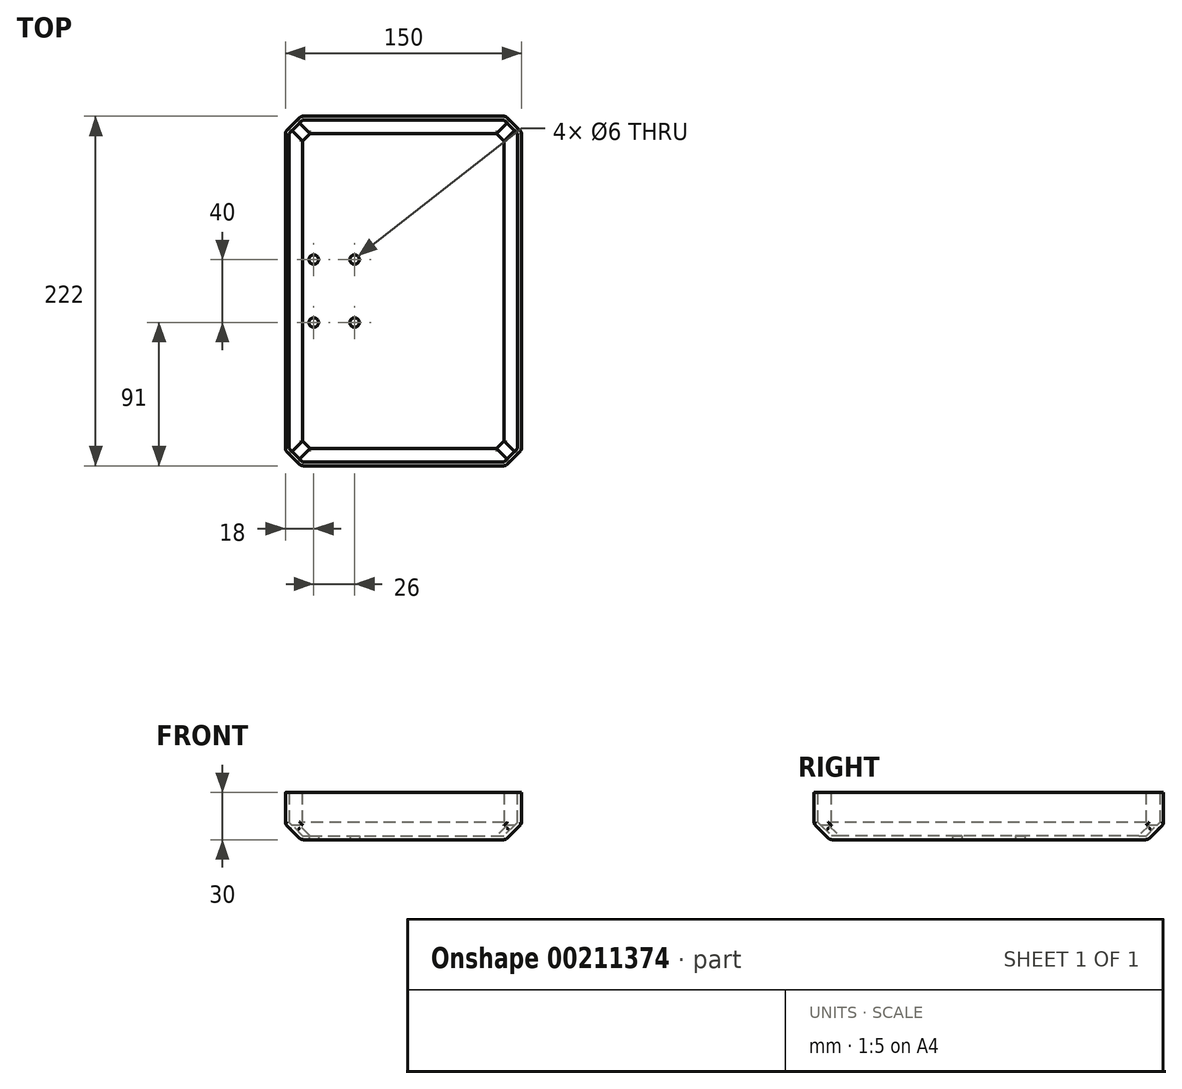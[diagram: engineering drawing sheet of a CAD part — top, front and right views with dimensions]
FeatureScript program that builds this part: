
annotation { "Feature Type Name" : "Feature", "Feature Type Description" : "" }
export const myFeature = defineFeature(function(context is Context, id is Id, definition is map)
    precondition{}
    {
        {
            var Q0;
            Q0=qCreatedBy(makeId("Front.planeOp"),FACE);
            var sketch = newSketch(context, id + "F0", { "sketchPlane" : qUnion([Q0])});
            skLineSegment(sketch, "E0.bottom", {"start": v(10, 0) * mm, "end": v(140, 0) * mm});
            skLineSegment(sketch, "E0.left", {"start": v(0, 10) * mm, "end": v(0, 30) * mm});
            skLineSegment(sketch, "E0.right", {"start": v(150, 10) * mm, "end": v(150, 30) * mm});
            skPoint(sketch, "E1.visualSharp", {"position": v(0, 0) * mm});
            skPoint(sketch, "E2.visualSharp", {"position": v(150, 0) * mm});
            skLineSegment(sketch, "E3", {"start": v(0, 30) * mm, "end": v(150, 30) * mm});
            skLineSegment(sketch, "E4", {"start": v(150, 10) * mm, "end": v(150, 0) * mm});
            skLineSegment(sketch, "E5", {"start": v(140, 0) * mm, "end": v(150, 0) * mm});
            skLineSegment(sketch, "E6", {"start": v(10, 0) * mm, "end": v(0, 0) * mm});
            skLineSegment(sketch, "E7", {"start": v(0, 10) * mm, "end": v(0, 0) * mm});
            skSolve(sketch);
        }
        {
            var Q0;
            Q0 = qSketchRegion(id + "F0", true);
            var Q1;
            Q1 = qConstructionFilter(qBodyType(qCreatedBy(id + "F0" ,EDGE), BodyType.WIRE), ConstructionObject.NO);
            extrude(context, id + "F1", {"entities" : qUnion([Q0]), "surfaceEntities" : qUnion([Q1]), "depth" : 222 * mm});
        }
        {
            var Q0;
            Q0=makeQuery(id+"F1.opExtrude","CAP_EDGE",EDGE,{"disambiguationData":[OSD([sQuery(id+"F0.wireOp",EDGE,"E0.left"),sQuery(id+"F0.wireOp",EDGE,"E7")])],"isStart":false});
            var Q1;
            Q1=makeQuery(id+"F1.opExtrude","CAP_EDGE",EDGE,{"disambiguationData":[OSD([sQuery(id+"F0.wireOp",EDGE,"E0.right"),sQuery(id+"F0.wireOp",EDGE,"E4")])],"isStart":false});
            var Q2;
            Q2=makeQuery(id+"F1.opExtrude","CAP_EDGE",EDGE,{"disambiguationData":[OSD([sQuery(id+"F0.wireOp",EDGE,"E0.right"),sQuery(id+"F0.wireOp",EDGE,"E4")])],"isStart":true});
            var Q3;
            Q3=makeQuery(id+"F1.opExtrude","CAP_EDGE",EDGE,{"disambiguationData":[OSD([sQuery(id+"F0.wireOp",EDGE,"E0.left"),sQuery(id+"F0.wireOp",EDGE,"E7")])],"isStart":true});
            chamfer(context, id + "F2", {"entities" : qUnion([Q0, Q1, Q2, Q3]), "width" : 10 * mm, "tangentPropagation" : true});
        }
        {
            var Q0;
            Q0=makeQuery(id+"F1.opExtrude","SWEPT_EDGE",EDGE,{"disambiguationData":[OSD([sQuery(id+"F0.wireOp",EDGE,"E4"),sQuery(id+"F0.wireOp",EDGE,"E5")])]});
            var Q1;
            Q1=makeQuery(id+"F1.opExtrude","CAP_EDGE",EDGE,{"disambiguationData":[OSD([sQuery(id+"F0.wireOp",EDGE,"E0.bottom"),sQuery(id+"F0.wireOp",EDGE,"E5"),sQuery(id+"F0.wireOp",EDGE,"E6")])],"isStart":false});
            var Q2;
            Q2=makeQuery(id+"F1.opExtrude","CAP_EDGE",EDGE,{"disambiguationData":[OSD([sQuery(id+"F0.wireOp",EDGE,"E0.bottom"),sQuery(id+"F0.wireOp",EDGE,"E5"),sQuery(id+"F0.wireOp",EDGE,"E6")])],"isStart":true});
            var Q3;
            Q3=makeQuery(id+"F1.opExtrude","SWEPT_EDGE",EDGE,{"disambiguationData":[OSD([sQuery(id+"F0.wireOp",EDGE,"E6"),sQuery(id+"F0.wireOp",EDGE,"E7")])]});
            chamfer(context, id + "F3", {"entities" : qUnion([Q0, Q1, Q2, Q3]), "width" : 10 * mm, "tangentPropagation" : true});
        }
        {
            var Q0;
            {var subQ0=sQuery(id+"F0.wireOp",EDGE,"E6");Q0=makeQuery(id+"F3.opChamfer","BLEND_EDGE",EDGE,{"blendedFrom":[makeQuery(id+"F1.opExtrude","SWEPT_EDGE",EDGE,{"disambiguationData":[OSD([subQ0,sQuery(id+"F0.wireOp",EDGE,"E7")])]}),makeQuery(id+"F1.opExtrude","CAP_EDGE",EDGE,{"disambiguationData":[OSD([sQuery(id+"F0.wireOp",EDGE,"E0.bottom"),sQuery(id+"F0.wireOp",EDGE,"E5"),subQ0])],"isStart":false})],"blendedInto":[]});}
            var Q1;
            {var subQ0=sQuery(id+"F0.wireOp",EDGE,"E5");Q1=makeQuery(id+"F3.opChamfer","BLEND_EDGE",EDGE,{"blendedFrom":[makeQuery(id+"F1.opExtrude","SWEPT_EDGE",EDGE,{"disambiguationData":[OSD([sQuery(id+"F0.wireOp",EDGE,"E4"),subQ0])]}),makeQuery(id+"F1.opExtrude","CAP_EDGE",EDGE,{"disambiguationData":[OSD([sQuery(id+"F0.wireOp",EDGE,"E0.bottom"),subQ0,sQuery(id+"F0.wireOp",EDGE,"E6")])],"isStart":false})],"blendedInto":[]});}
            var Q2;
            {var subQ0=sQuery(id+"F0.wireOp",EDGE,"E5");Q2=makeQuery(id+"F3.opChamfer","BLEND_EDGE",EDGE,{"blendedFrom":[makeQuery(id+"F1.opExtrude","SWEPT_EDGE",EDGE,{"disambiguationData":[OSD([sQuery(id+"F0.wireOp",EDGE,"E4"),subQ0])]}),makeQuery(id+"F1.opExtrude","CAP_EDGE",EDGE,{"disambiguationData":[OSD([sQuery(id+"F0.wireOp",EDGE,"E0.bottom"),subQ0,sQuery(id+"F0.wireOp",EDGE,"E6")])],"isStart":true})],"blendedInto":[]});}
            var Q3;
            {var subQ0=sQuery(id+"F0.wireOp",EDGE,"E6");Q3=makeQuery(id+"F3.opChamfer","BLEND_EDGE",EDGE,{"blendedFrom":[makeQuery(id+"F1.opExtrude","SWEPT_EDGE",EDGE,{"disambiguationData":[OSD([subQ0,sQuery(id+"F0.wireOp",EDGE,"E7")])]}),makeQuery(id+"F1.opExtrude","CAP_EDGE",EDGE,{"disambiguationData":[OSD([sQuery(id+"F0.wireOp",EDGE,"E0.bottom"),sQuery(id+"F0.wireOp",EDGE,"E5"),subQ0])],"isStart":true})],"blendedInto":[]});}
            chamfer(context, id + "F4", {"entities" : qUnion([Q0, Q1, Q2, Q3]), "width" : 8 * mm, "tangentPropagation" : true});
        }
        {
            var Q0;
            Q0=makeQuery(id+"F1.opExtrude","SWEPT_FACE",FACE,{"disambiguationData":[OSD([sQuery(id+"F0.wireOp",EDGE,"E3")])]});
            shell(context, id + "F5", {"entities" : qUnion([Q0]), "thickness" : 2.5 * mm});
        }
        {
            var Q0;
            Q0=makeQuery(id+"F1.opExtrude","SWEPT_FACE",FACE,{"disambiguationData":[OSD([sQuery(id+"F0.wireOp",EDGE,"E0.bottom"),sQuery(id+"F0.wireOp",EDGE,"E5"),sQuery(id+"F0.wireOp",EDGE,"E6")])]});
            var Q1;
            Q1=makeQuery(id+"F3.opChamfer","BLEND_FACE",FACE,{"disambiguationData":[OSD([sQuery(id+"F0.wireOp",EDGE,"E6"),sQuery(id+"F0.wireOp",EDGE,"E7")])]});
            var Q2;
            {var subQ0=sQuery(id+"F0.wireOp",EDGE,"E6");var subQ1=sQuery(id+"F0.wireOp",EDGE,"E5");var subQ2=sQuery(id+"F0.wireOp",EDGE,"E0.bottom");var subQ3=sQuery(id+"F0.wireOp",EDGE,"E7");Q2=makeQuery(id+"F4.opChamfer","BLEND_FACE",FACE,{"disambiguationData":[OSD([subQ2,subQ1,subQ0,subQ3]),TDD([makeQuery(id+"F3.opChamfer","BLEND_EDGE",EDGE,{"blendedFrom":[makeQuery(id+"F1.opExtrude","SWEPT_EDGE",EDGE,{"disambiguationData":[OSD([subQ0,subQ3])]}),makeQuery(id+"F1.opExtrude","CAP_EDGE",EDGE,{"disambiguationData":[OSD([subQ2,subQ1,subQ0])],"isStart":false})],"blendedInto":[]})])]});}
            var Q3;
            {var subQ0=sQuery(id+"F0.wireOp",EDGE,"E6");var subQ1=sQuery(id+"F0.wireOp",EDGE,"E5");var subQ2=sQuery(id+"F0.wireOp",EDGE,"E0.bottom");Q3=makeQuery(id+"F3.opChamfer","BLEND_FACE",FACE,{"disambiguationData":[OSD([subQ2,subQ1,subQ0]),TDD([makeQuery(id+"F1.opExtrude","CAP_EDGE",EDGE,{"disambiguationData":[OSD([subQ2,subQ1,subQ0])],"isStart":false})])]});}
            var Q4;
            {var subQ0=sQuery(id+"F0.wireOp",EDGE,"E6");var subQ1=sQuery(id+"F0.wireOp",EDGE,"E5");var subQ2=sQuery(id+"F0.wireOp",EDGE,"E0.bottom");var subQ3=sQuery(id+"F0.wireOp",EDGE,"E4");Q4=makeQuery(id+"F4.opChamfer","BLEND_FACE",FACE,{"disambiguationData":[OSD([subQ2,subQ3,subQ1,subQ0]),TDD([makeQuery(id+"F3.opChamfer","BLEND_EDGE",EDGE,{"blendedFrom":[makeQuery(id+"F1.opExtrude","SWEPT_EDGE",EDGE,{"disambiguationData":[OSD([subQ3,subQ1])]}),makeQuery(id+"F1.opExtrude","CAP_EDGE",EDGE,{"disambiguationData":[OSD([subQ2,subQ1,subQ0])],"isStart":false})],"blendedInto":[]})])]});}
            var Q5;
            Q5=makeQuery(id+"F3.opChamfer","BLEND_FACE",FACE,{"disambiguationData":[OSD([sQuery(id+"F0.wireOp",EDGE,"E4"),sQuery(id+"F0.wireOp",EDGE,"E5")])]});
            var Q6;
            {var subQ0=sQuery(id+"F0.wireOp",EDGE,"E6");var subQ1=sQuery(id+"F0.wireOp",EDGE,"E5");var subQ2=sQuery(id+"F0.wireOp",EDGE,"E0.bottom");var subQ3=sQuery(id+"F0.wireOp",EDGE,"E4");Q6=makeQuery(id+"F4.opChamfer","BLEND_FACE",FACE,{"disambiguationData":[OSD([subQ2,subQ3,subQ1,subQ0]),TDD([makeQuery(id+"F3.opChamfer","BLEND_EDGE",EDGE,{"blendedFrom":[makeQuery(id+"F1.opExtrude","SWEPT_EDGE",EDGE,{"disambiguationData":[OSD([subQ3,subQ1])]}),makeQuery(id+"F1.opExtrude","CAP_EDGE",EDGE,{"disambiguationData":[OSD([subQ2,subQ1,subQ0])],"isStart":true})],"blendedInto":[]})])]});}
            var Q7;
            {var subQ0=sQuery(id+"F0.wireOp",EDGE,"E6");var subQ1=sQuery(id+"F0.wireOp",EDGE,"E5");var subQ2=sQuery(id+"F0.wireOp",EDGE,"E0.bottom");Q7=makeQuery(id+"F3.opChamfer","BLEND_FACE",FACE,{"disambiguationData":[OSD([subQ2,subQ1,subQ0]),TDD([makeQuery(id+"F1.opExtrude","CAP_EDGE",EDGE,{"disambiguationData":[OSD([subQ2,subQ1,subQ0])],"isStart":true})])]});}
            var Q8;
            {var subQ0=sQuery(id+"F0.wireOp",EDGE,"E6");var subQ1=sQuery(id+"F0.wireOp",EDGE,"E5");var subQ2=sQuery(id+"F0.wireOp",EDGE,"E0.bottom");var subQ3=sQuery(id+"F0.wireOp",EDGE,"E7");Q8=makeQuery(id+"F4.opChamfer","BLEND_FACE",FACE,{"disambiguationData":[OSD([subQ2,subQ1,subQ0,subQ3]),TDD([makeQuery(id+"F3.opChamfer","BLEND_EDGE",EDGE,{"blendedFrom":[makeQuery(id+"F1.opExtrude","SWEPT_EDGE",EDGE,{"disambiguationData":[OSD([subQ0,subQ3])]}),makeQuery(id+"F1.opExtrude","CAP_EDGE",EDGE,{"disambiguationData":[OSD([subQ2,subQ1,subQ0])],"isStart":true})],"blendedInto":[]})])]});}
            var Q9;
            {var subQ0=sQuery(id+"F0.wireOp",EDGE,"E7");var subQ1=sQuery(id+"F0.wireOp",EDGE,"E0.left");Q9=makeQuery(id+"F2.opChamfer","BLEND_EDGE",EDGE,{"blendedFrom":[makeQuery(id+"F1.opExtrude","CAP_EDGE",EDGE,{"disambiguationData":[OSD([subQ1,subQ0])],"isStart":true}),makeQuery(id+"F1.opExtrude","SWEPT_FACE",FACE,{"disambiguationData":[OSD([subQ1,subQ0])]})],"blendedInto":[makeQuery(id+"F1.opExtrude","SWEPT_FACE",FACE,{"disambiguationData":[OSD([subQ1,subQ0])]})]});}
            var Q10;
            {var subQ0=sQuery(id+"F0.wireOp",EDGE,"E7");var subQ1=sQuery(id+"F0.wireOp",EDGE,"E0.left");Q10=makeQuery(id+"F2.opChamfer","BLEND_EDGE",EDGE,{"blendedFrom":[makeQuery(id+"F1.opExtrude","CAP_EDGE",EDGE,{"disambiguationData":[OSD([subQ1,subQ0])],"isStart":true}),makeQuery(id+"F1.opExtrude","CAP_FACE",FACE,{"disambiguationData":[OSD([sQuery(id+"F0.wireOp",EDGE,"E0.bottom"),subQ1,sQuery(id+"F0.wireOp",EDGE,"E0.right"),sQuery(id+"F0.wireOp",EDGE,"E3"),sQuery(id+"F0.wireOp",EDGE,"E4"),sQuery(id+"F0.wireOp",EDGE,"E5"),sQuery(id+"F0.wireOp",EDGE,"E6"),subQ0])],"isStart":true})],"blendedInto":[makeQuery(id+"F1.opExtrude","CAP_FACE",FACE,{"disambiguationData":[OSD([sQuery(id+"F0.wireOp",EDGE,"E0.bottom"),subQ1,sQuery(id+"F0.wireOp",EDGE,"E0.right"),sQuery(id+"F0.wireOp",EDGE,"E3"),sQuery(id+"F0.wireOp",EDGE,"E4"),sQuery(id+"F0.wireOp",EDGE,"E5"),sQuery(id+"F0.wireOp",EDGE,"E6"),subQ0])],"isStart":true})]});}
            var Q11;
            {var subQ0=sQuery(id+"F0.wireOp",EDGE,"E7");var subQ1=sQuery(id+"F0.wireOp",EDGE,"E0.left");Q11=makeQuery(id+"F2.opChamfer","BLEND_EDGE",EDGE,{"blendedFrom":[makeQuery(id+"F1.opExtrude","CAP_EDGE",EDGE,{"disambiguationData":[OSD([subQ1,subQ0])],"isStart":false}),makeQuery(id+"F1.opExtrude","SWEPT_FACE",FACE,{"disambiguationData":[OSD([subQ1,subQ0])]})],"blendedInto":[makeQuery(id+"F1.opExtrude","SWEPT_FACE",FACE,{"disambiguationData":[OSD([subQ1,subQ0])]})]});}
            var Q12;
            {var subQ0=sQuery(id+"F0.wireOp",EDGE,"E7");var subQ1=sQuery(id+"F0.wireOp",EDGE,"E0.left");Q12=makeQuery(id+"F2.opChamfer","BLEND_EDGE",EDGE,{"blendedFrom":[makeQuery(id+"F1.opExtrude","CAP_EDGE",EDGE,{"disambiguationData":[OSD([subQ1,subQ0])],"isStart":false}),makeQuery(id+"F1.opExtrude","CAP_FACE",FACE,{"disambiguationData":[OSD([sQuery(id+"F0.wireOp",EDGE,"E0.bottom"),subQ1,sQuery(id+"F0.wireOp",EDGE,"E0.right"),sQuery(id+"F0.wireOp",EDGE,"E3"),sQuery(id+"F0.wireOp",EDGE,"E4"),sQuery(id+"F0.wireOp",EDGE,"E5"),sQuery(id+"F0.wireOp",EDGE,"E6"),subQ0])],"isStart":false})],"blendedInto":[makeQuery(id+"F1.opExtrude","CAP_FACE",FACE,{"disambiguationData":[OSD([sQuery(id+"F0.wireOp",EDGE,"E0.bottom"),subQ1,sQuery(id+"F0.wireOp",EDGE,"E0.right"),sQuery(id+"F0.wireOp",EDGE,"E3"),sQuery(id+"F0.wireOp",EDGE,"E4"),sQuery(id+"F0.wireOp",EDGE,"E5"),sQuery(id+"F0.wireOp",EDGE,"E6"),subQ0])],"isStart":false})]});}
            var Q13;
            {var subQ0=sQuery(id+"F0.wireOp",EDGE,"E4");var subQ1=sQuery(id+"F0.wireOp",EDGE,"E0.right");Q13=makeQuery(id+"F2.opChamfer","BLEND_EDGE",EDGE,{"blendedFrom":[makeQuery(id+"F1.opExtrude","CAP_EDGE",EDGE,{"disambiguationData":[OSD([subQ1,subQ0])],"isStart":false}),makeQuery(id+"F1.opExtrude","CAP_FACE",FACE,{"disambiguationData":[OSD([sQuery(id+"F0.wireOp",EDGE,"E0.bottom"),sQuery(id+"F0.wireOp",EDGE,"E0.left"),subQ1,sQuery(id+"F0.wireOp",EDGE,"E3"),subQ0,sQuery(id+"F0.wireOp",EDGE,"E5"),sQuery(id+"F0.wireOp",EDGE,"E6"),sQuery(id+"F0.wireOp",EDGE,"E7")])],"isStart":false})],"blendedInto":[makeQuery(id+"F1.opExtrude","CAP_FACE",FACE,{"disambiguationData":[OSD([sQuery(id+"F0.wireOp",EDGE,"E0.bottom"),sQuery(id+"F0.wireOp",EDGE,"E0.left"),subQ1,sQuery(id+"F0.wireOp",EDGE,"E3"),subQ0,sQuery(id+"F0.wireOp",EDGE,"E5"),sQuery(id+"F0.wireOp",EDGE,"E6"),sQuery(id+"F0.wireOp",EDGE,"E7")])],"isStart":false})]});}
            var Q14;
            {var subQ0=sQuery(id+"F0.wireOp",EDGE,"E4");var subQ1=sQuery(id+"F0.wireOp",EDGE,"E0.right");Q14=makeQuery(id+"F2.opChamfer","BLEND_EDGE",EDGE,{"blendedFrom":[makeQuery(id+"F1.opExtrude","CAP_EDGE",EDGE,{"disambiguationData":[OSD([subQ1,subQ0])],"isStart":false}),makeQuery(id+"F1.opExtrude","SWEPT_FACE",FACE,{"disambiguationData":[OSD([subQ1,subQ0])]})],"blendedInto":[makeQuery(id+"F1.opExtrude","SWEPT_FACE",FACE,{"disambiguationData":[OSD([subQ1,subQ0])]})]});}
            var Q15;
            {var subQ0=sQuery(id+"F0.wireOp",EDGE,"E4");var subQ1=sQuery(id+"F0.wireOp",EDGE,"E0.right");Q15=makeQuery(id+"F2.opChamfer","BLEND_EDGE",EDGE,{"blendedFrom":[makeQuery(id+"F1.opExtrude","CAP_EDGE",EDGE,{"disambiguationData":[OSD([subQ1,subQ0])],"isStart":true}),makeQuery(id+"F1.opExtrude","SWEPT_FACE",FACE,{"disambiguationData":[OSD([subQ1,subQ0])]})],"blendedInto":[makeQuery(id+"F1.opExtrude","SWEPT_FACE",FACE,{"disambiguationData":[OSD([subQ1,subQ0])]})]});}
            var Q16;
            {var subQ0=sQuery(id+"F0.wireOp",EDGE,"E4");var subQ1=sQuery(id+"F0.wireOp",EDGE,"E0.right");Q16=makeQuery(id+"F2.opChamfer","BLEND_EDGE",EDGE,{"blendedFrom":[makeQuery(id+"F1.opExtrude","CAP_EDGE",EDGE,{"disambiguationData":[OSD([subQ1,subQ0])],"isStart":true}),makeQuery(id+"F1.opExtrude","CAP_FACE",FACE,{"disambiguationData":[OSD([sQuery(id+"F0.wireOp",EDGE,"E0.bottom"),sQuery(id+"F0.wireOp",EDGE,"E0.left"),subQ1,sQuery(id+"F0.wireOp",EDGE,"E3"),subQ0,sQuery(id+"F0.wireOp",EDGE,"E5"),sQuery(id+"F0.wireOp",EDGE,"E6"),sQuery(id+"F0.wireOp",EDGE,"E7")])],"isStart":true})],"blendedInto":[makeQuery(id+"F1.opExtrude","CAP_FACE",FACE,{"disambiguationData":[OSD([sQuery(id+"F0.wireOp",EDGE,"E0.bottom"),sQuery(id+"F0.wireOp",EDGE,"E0.left"),subQ1,sQuery(id+"F0.wireOp",EDGE,"E3"),subQ0,sQuery(id+"F0.wireOp",EDGE,"E5"),sQuery(id+"F0.wireOp",EDGE,"E6"),sQuery(id+"F0.wireOp",EDGE,"E7")])],"isStart":true})]});}
            fillet(context, id + "F6", {"entities" : qUnion([Q0, Q1, Q2, Q3, Q4, Q5, Q6, Q7, Q8, Q9, Q10, Q11, Q12, Q13, Q14, Q15, Q16]), "radius" : 3 * mm, "tangentPropagation" : true, "allowEdgeOverflow" : false});
        }
        {
            var Q0;
            Q0=makeQuery(id+"F1.opExtrude","SWEPT_FACE",FACE,{"disambiguationData":[OSD([sQuery(id+"F0.wireOp",EDGE,"E0.bottom")])]});
            var sketch = newSketch(context, id + "F7", { "sketchPlane" : qUnion([Q0])});
            skCircle(sketch, "E8", {"center": v(44, 131) * mm, "radius": 3 * mm});
            skCircle(sketch, "E9", {"center": v(18, 131) * mm, "radius": 3 * mm});
            skCircle(sketch, "E10", {"center": v(44, 91) * mm, "radius": 3 * mm});
            skCircle(sketch, "E11", {"center": v(18, 91) * mm, "radius": 3 * mm});
            skSolve(sketch);
        }
        {
            var Q0;
            Q0=makeQuery(id+"F7.imprint","IMPRINT",FACE,{"disambiguationData":[TD([[makeQuery(id+"F7.imprint","IMPRINT",EDGE,{"derivedFrom":sQuery(id+"F7.wireOp",EDGE,"E9")}),1.0]])]});
            var Q1;
            Q1=makeQuery(id+"F7.imprint","IMPRINT",FACE,{"disambiguationData":[TD([[makeQuery(id+"F7.imprint","IMPRINT",EDGE,{"derivedFrom":sQuery(id+"F7.wireOp",EDGE,"E8")}),1.0]])]});
            var Q2;
            Q2=makeQuery(id+"F7.imprint","IMPRINT",FACE,{"disambiguationData":[TD([[makeQuery(id+"F7.imprint","IMPRINT",EDGE,{"derivedFrom":sQuery(id+"F7.wireOp",EDGE,"E10")}),1.0]])]});
            var Q3;
            Q3=makeQuery(id+"F7.imprint","IMPRINT",FACE,{"disambiguationData":[TD([[makeQuery(id+"F7.imprint","IMPRINT",EDGE,{"derivedFrom":sQuery(id+"F7.wireOp",EDGE,"E11")}),1.0]])]});
            extrude(context, id + "F8", {"entities" : qUnion([Q0, Q1, Q2, Q3]), "operationType" : NewBodyOperationType.REMOVE, "endBound" : BoundingType.THROUGH_ALL, "oppositeDirection" : true, "depth" : 25 * mm});
        }
    });
